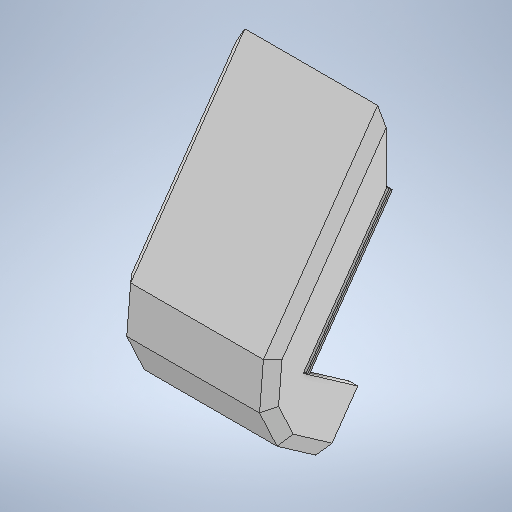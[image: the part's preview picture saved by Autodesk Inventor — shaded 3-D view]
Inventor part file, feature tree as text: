
AUTODESK INVENTOR PART (.ipt)
format: ipt  version: 2025.2 (Build 292293000, 293)  size: 847,872 bytes
history: native  units: in
note: dims shown in document units (in); Inventor stores cm internally (conversion verified against a paired STEP export)
features: sketch x42, extrude x38, projected_geometry x9, plane x8, move_body x1, chamfer x1, fillet x1, hole x1
ambient origin geometry x8: Origin, YZ Plane, XZ Plane, XY Plane, X Axis, Y Axis, Z Axis, Center Point
bodies: Solid1 (feature_tree)
feature tree (101):
  extrude  "Extrusion1"  Depth=0.1969in TaperAngle=0.0deg
  move_body  "Move Body1"
  plane  "Work Plane1"
  sketch  "Sketch5"  dims[d5=1.7717in d6=1.7717in d7=1.7717in d8=1.7717in d9=0.8108in d10=90.0deg d11=0.0787in d12=0.3701in d13=0.4252in d14=0.1362in d15=-0.0984in d16=-0.0591in d17=0.0in]
  plane  "Work Plane2"
  extrude  "Extrusion4"  TaperAngle=0.0deg  [1 undecoded]
  extrude  "Extrusion6"  Depth=0.2405in
  extrude  "Extrusion8"  Depth=2.5591in TaperAngle=0.0deg
  chamfer  "Chamfer1"  [1 undecoded]
  extrude  "Extrusion11"  Depth=0.2362in
  plane  "Work Plane3"
  plane  "Work Plane7"
  extrude  "Extrusion22"  Depth=0.1969in TaperAngle=0.0deg
  extrude  "Extrusion25"  Depth=0.5027in
  extrude  "Extrusion26"  Depth=0.5027in
  sketch  "Sketch33"  dims[d96=0.2362in d97=0.0in d100=3.6403in]
  extrude  "Extrusion27"  Depth=0.2362in TaperAngle=0.0deg
  extrude  "Extrusion28"  Depth=3.6403in
  sketch  "Sketch36"  dims[d123=0.9331in d124=0.9712in d125=0.0in]
  extrude  "Extrusion29"  Depth=1.9685in
  extrude  "Extrusion30"  Depth=0.1575in
  extrude  "Extrusion31"  Depth=0.9712in TaperAngle=0.0deg
  sketch  "Sketch39"  dims[d138=0.4331in d139=0.1181in d140=0.0in]
  extrude  "Extrusion32"  Depth=11.3469in TaperAngle=0.0deg
  fillet  "Fillet1"  Radius=11.3469in
  extrude  "Extrusion33"  Depth=0.4331in
  extrude  "Extrusion34"  Depth=0.1181in TaperAngle=0.0deg
  extrude  "Extrusion35"  Depth=0.0787in
  plane  "Work Plane8"
  sketch  "Sketch45"  dims[d160=0.1181in d161=0.0in d162=0.1969in d163=0.0in d164=0.1181in d165=0.0in]
  extrude  "Extrusion37"  Depth=0.2756in
  extrude  "Extrusion38"  Depth=0.1181in TaperAngle=0.0deg
  extrude  "Extrusion40"  Depth=0.1181in
  extrude  "Extrusion41"  Depth=0.1181in TaperAngle=0.0deg
  extrude  "Extrusion43"  Depth=4.7244in TaperAngle=0.0deg
  extrude  "Extrusion44"  Depth=0.7313in TaperAngle=0.0deg
  extrude  "Extrusion46"  TaperAngle=0.0deg  [1 undecoded]
  extrude  "Extrusion48"  Depth=1.1024in
  extrude  "Extrusion50"  Depth=0.0394in TaperAngle=0.0deg
  extrude  "Extrusion51"  Depth=5.8937in TaperAngle=0.0deg
  extrude  "Extrusion52"  Depth=0.0591in
  extrude  "Extrusion53"  Depth=0.0394in
  plane  "Work Plane9"
  extrude  "Extrusion55"  Depth=0.0787in TaperAngle=0.0deg
  extrude  "Extrusion56"  Depth=0.5917in TaperAngle=0.0deg
  plane  "Work Plane10"
  extrude  "Extrusion57"  TaperAngle=120.0deg  [1 undecoded]
  plane  "Work Plane11"
  extrude  "Extrusion58"  TaperAngle=0.0deg  [1 undecoded]
  extrude  "Extrusion59"  Depth=1.1811in TaperAngle=0.0deg
  extrude  "Extrusion60"  TaperAngle=0.0deg  [1 undecoded]
  extrude  "Extrusion61"  TaperAngle=0.0deg  [1 undecoded]
  extrude  "Extrusion62"  Depth=0.2362in TaperAngle=0.0deg
  extrude  "Extrusion63"  Depth=0.2362in TaperAngle=0.0deg
  sketch  "Sketch1"  dims[d1=0.5512in d2=0.1969in d3=0.0in]
  sketch  "Sketch6"  dims[d18=0.2749in d24=0.2405in]
  sketch  "Sketch8"  dims[d25=2.7559in d26=0.0in d29=2.5591in d30=0.0in d36=0.0in d37=0.0in]
  sketch  "Sketch12"  dims[d42=0.2362in d43=0.2362in]
  sketch  "Sketch15"  dims[d52=0.2362in d53=0.0787in d54=45.0deg d55=0.1969in d56=0.0in]
  sketch  "Sketch28"  dims[d76=0.5027in d77=0.5027in]
  sketch  "Sketch31"  dims[d78=0.5027in d79=0.5027in]
  sketch  "Sketch32"  dims[d83=0.0in d84=0.0in d94=0.2362in d95=0.0in]
  sketch  "Sketch34"  dims[d101=2.7717in d112=1.9685in]
  sketch  "Sketch35"  dims[d113=0.6299in d114=0.0in d115=0.1575in d117=0.1575in d121=1.9685in d122=0.7874in]
  sketch  "Sketch37"  dims[d126=0.5906in d127=0.0in d128=11.3469in d129=0.0in d130=11.3469in d131=0.0in]
  sketch  "Sketch38"  dims[d136=0.4331in d137=0.4331in]
  sketch  "Sketch40"  dims[d141=0.6299in d142=0.0787in]
  sketch  "Sketch41"  dims[d147=0.2756in d149=0.2756in]
  sketch  "Sketch42"  dims[d150=0.0in d151=0.0in d154=0.1181in d155=0.0in]
  sketch  "Sketch44"  dims[d156=0.1181in d157=0.0in d158=0.5906in]
  projected_geometry  "Projected Loop2"
  projected_geometry  "Projected Loop3"
  projected_geometry  "Projected Loop5"
  sketch  "Sketch47"  dims[d168=0.5906in d169=0.0in d170=4.7244in d171=0.0in]
  sketch  "Sketch49"  dims[d174=0.0in d175=0.0in d176=0.7313in d177=0.0in]
  sketch  "Sketch50"  dims[d186=0.0in d187=0.0in d188=0.0in d189=0.0in]
  sketch  "Sketch52"  dims[d194=0.0in d195=0.0in d196=1.1024in]
  sketch  "Sketch53"  dims[d197=0.5906in d200=0.0394in d201=0.0in]
  sketch  "Sketch56"  dims[d218=0.0in d219=0.0in d220=5.8937in d221=0.0in]
  sketch  "Sketch59"  dims[d226=0.0787in d227=0.0591in]
  sketch  "Sketch60"  dims[d228=0.0394in d229=0.0394in]
  sketch  "Sketch61"  dims[d230=0.0787in d231=3.3754in d232=0.0in]
  sketch  "Sketch62"  dims[d233=0.9963in d234=0.5917in d235=0.0in]
  sketch  "Sketch63"  dims[d236=2.0564in d238=120.0deg]
  projected_geometry  "Projected Loop8"
  sketch  "Sketch65"  dims[d241=1.378in d242=0.0in d243=0.0in d244=0.0in]
  projected_geometry  "Projected Loop9"
  sketch  "Sketch67"  dims[d245=120.0deg d246=1.1811in d247=0.0in]
  sketch  "Sketch68"  dims[d248=120.0deg d249=0.0in d250=0.0in]
  projected_geometry  "Projected Loop10"
  sketch  "Sketch69"  dims[d251=0.7874in d252=0.0in d253=0.0in d254=0.0in]
  sketch  "Sketch70"  dims[d255=0.2362in d256=0.0in d257=0.2362in d258=0.0in]
  projected_geometry  "Projected Loop11"
  sketch  "Sketch71"  dims[d259=0.2362in d260=0.5118in d261=0.0in]
  projected_geometry  "Projected Loop12"
  sketch  "Sketch72"  dims[d38=0.0197in d39=0.0344in]
  sketch  "Sketch73"  dims[d57=0.0197in]
  sketch  "Sketch74"  dims[d58=0.0344in d59=0.0197in d60=0.0344in d81=0.0197in d82=0.0344in d159=0.0344in d178=0.0in d179=0.0in d180=0.0in d181=0.0in d202=0.0197in d203=0.0344in d222=0.0197in d223=0.0344in]
  projected_geometry  "Projected Loop13"
  sketch  "Sketch2"  dims[d4=0.315in]
  hole  "Hole1"  [1 undecoded]
note: 8 required parameter values undecoded (feature->parameter linkage not recoverable at this tier; creation-order binding heuristic only, values carry confidence <= 0.55)
